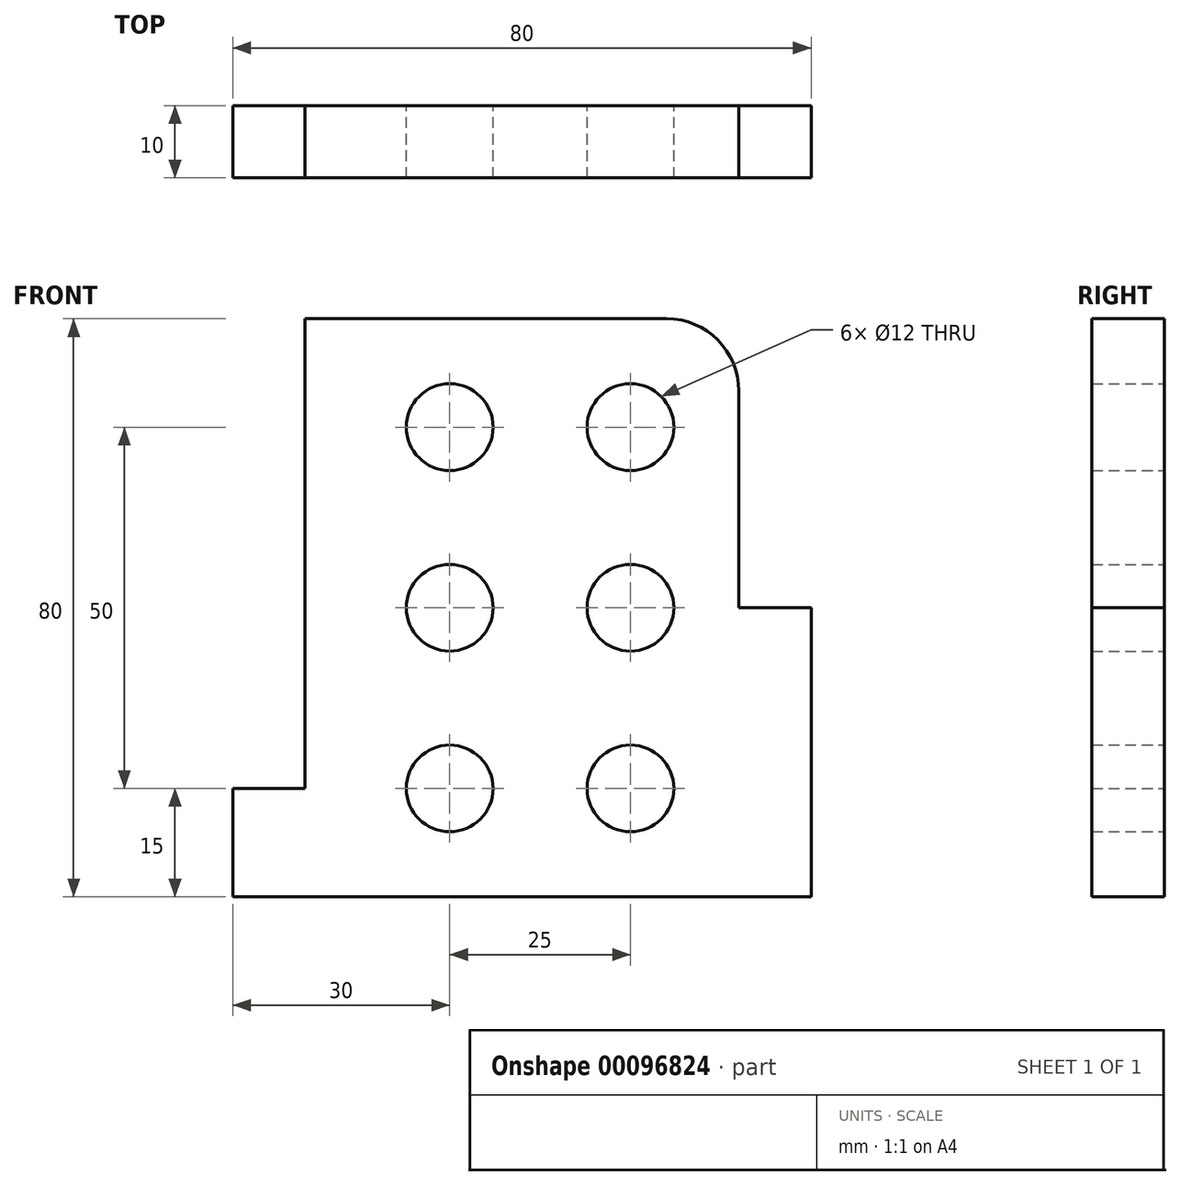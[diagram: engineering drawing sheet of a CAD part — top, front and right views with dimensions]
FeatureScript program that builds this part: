
annotation { "Feature Type Name" : "Feature", "Feature Type Description" : "" }
export const myFeature = defineFeature(function(context is Context, id is Id, definition is map)
    precondition{}
    {
        {
            var Q0;
            Q0=qCreatedBy(makeId("Front.planeOp"),FACE);
            var sketch = newSketch(context, id + "F0", { "sketchPlane" : qUnion([Q0])});
            skLineSegment(sketch, "E0", {"start": v(0, 0) * mm, "end": v(80, 0) * mm});
            skLineSegment(sketch, "E1", {"start": v(80, 0) * mm, "end": v(80, 40) * mm});
            skLineSegment(sketch, "E2", {"start": v(80, 40) * mm, "end": v(70, 40) * mm});
            skLineSegment(sketch, "E3", {"start": v(70, 40) * mm, "end": v(70, 70) * mm});
            skLineSegment(sketch, "E4", {"start": v(60, 80) * mm, "end": v(10, 80) * mm});
            skLineSegment(sketch, "E5", {"start": v(10, 80) * mm, "end": v(10, 15) * mm});
            skLineSegment(sketch, "E6", {"start": v(10, 15) * mm, "end": v(0, 15) * mm});
            skLineSegment(sketch, "E7", {"start": v(0, 15) * mm, "end": v(0, 0) * mm});
            skPoint(sketch, "E8.visualSharp", {"position": v(70, 80) * mm});
            skArc(sketch, "E8.filletArc", {"start": v(70, 70) * mm, "mid": v(67.07, 77.07) * mm, "end": v(60, 80) * mm});
            skCircle(sketch, "E9", {"center": v(30, 15) * mm, "radius": 6 * mm});
            skCircle(sketch, "E10", {"center": v(55, 15) * mm, "radius": 6 * mm});
            skCircle(sketch, "E11", {"center": v(30, 40) * mm, "radius": 6 * mm});
            skCircle(sketch, "E12", {"center": v(55, 40) * mm, "radius": 6 * mm});
            skCircle(sketch, "E13", {"center": v(30, 65) * mm, "radius": 6 * mm});
            skCircle(sketch, "E14", {"center": v(55, 65) * mm, "radius": 6 * mm});
            skSolve(sketch);
        }
        {
            var Q0;
            Q0 = qSketchRegion(id + "F0", true);
            extrude(context, id + "F1", {"entities" : qUnion([Q0]), "depth" : 10 * mm});
        }
    });
